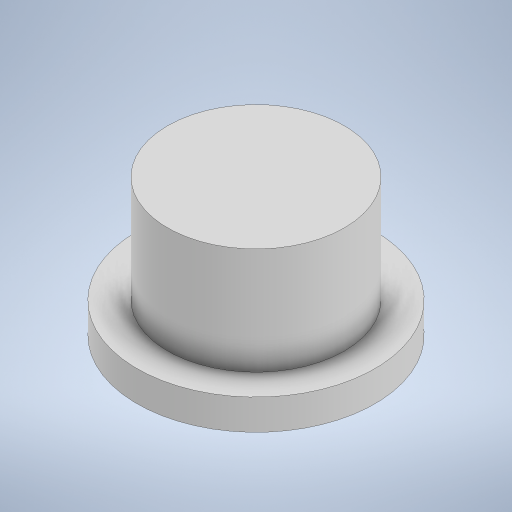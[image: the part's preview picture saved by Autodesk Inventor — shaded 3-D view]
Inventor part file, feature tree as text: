
AUTODESK INVENTOR PART (.ipt)
format: ipt  version: 2023 (Build 270158000, 158)  size: 228,864 bytes
history: native  units: in
note: dims shown in document units (in); Inventor stores cm internally (conversion verified against a paired STEP export)
features: extrude x2, sketch x1
ambient origin geometry x8: Origin, YZ Plane, XZ Plane, XY Plane, X Axis, Y Axis, Z Axis, Center Point
bodies: Solid1 (feature_tree)
feature tree (3):
  sketch  "Sketch1"  dims[d0=0.29in d1=0.39in d2=0.225in d3=0.0in d4=0.05in d5=0.0in]
  extrude  "Extrusion1"  Depth=0.05in
  extrude  "Extrusion2"  Depth=0.225in TaperAngle=0.0deg
